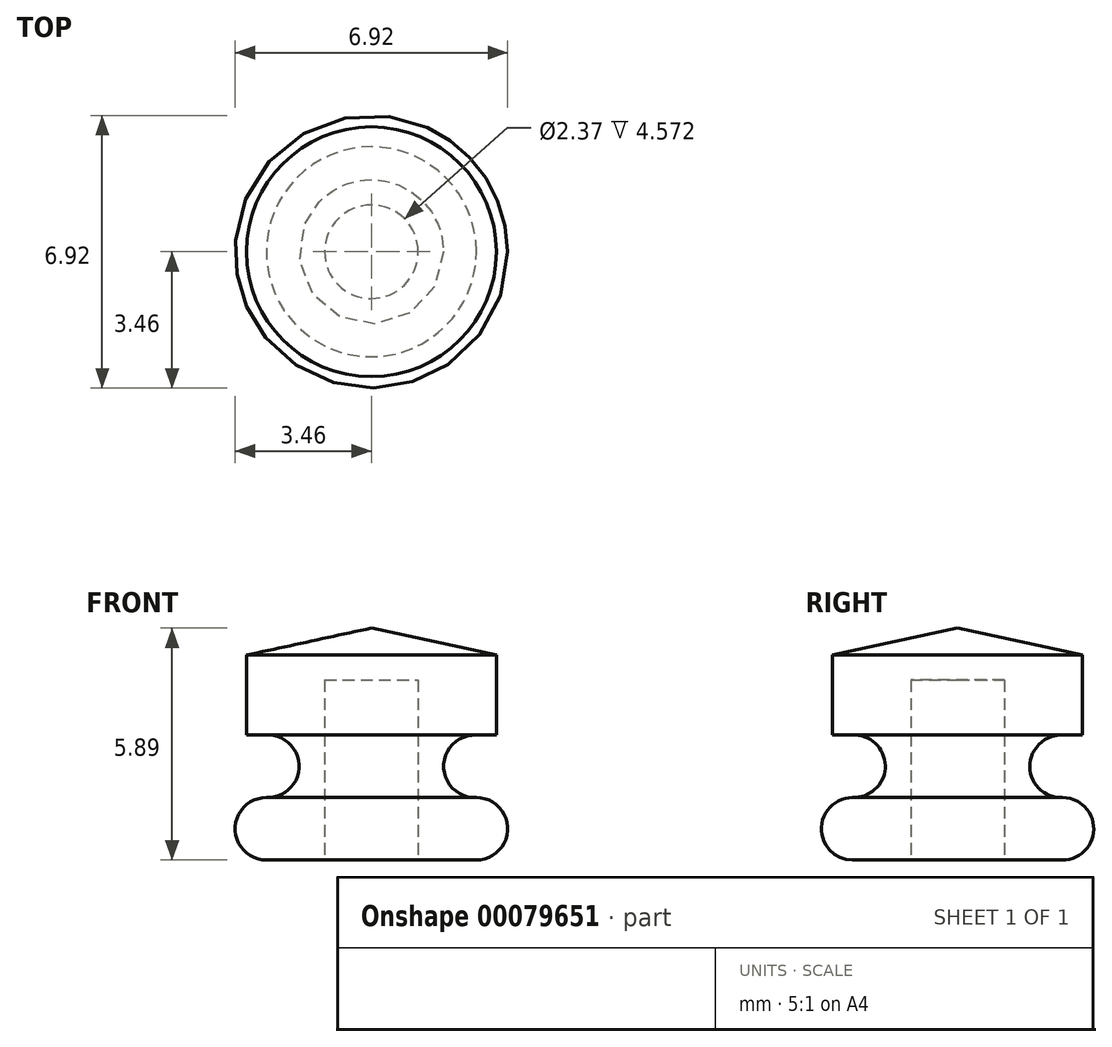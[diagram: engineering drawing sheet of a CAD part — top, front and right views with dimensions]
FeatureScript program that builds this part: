
annotation { "Feature Type Name" : "Feature", "Feature Type Description" : "" }
export const myFeature = defineFeature(function(context is Context, id is Id, definition is map)
    precondition{}
    {
        {
            var Q0;
            Q0=qCreatedBy(makeId("Front.planeOp"),FACE);
            var sketch = newSketch(context, id + "F0", { "sketchPlane" : qUnion([Q0])});
            skLineSegment(sketch, "E0", {"start": v(0, 13.12) * mm, "end": v(0, -12.35) * mm, "construction": true});
            skLineSegment(sketch, "E1", {"start": v(0, 1.69) * mm, "end": v(0, -4.2) * mm});
            skLineSegment(sketch, "E2", {"start": v(0, -4.2) * mm, "end": v(-2.67, -4.2) * mm});
            skArc(sketch, "E3", {"start": v(-2.67, -2.62) * mm, "mid": v(-3.46, -3.4) * mm, "end": v(-2.67, -4.2) * mm});
            skArc(sketch, "E4", {"start": v(-2.67, -2.62) * mm, "mid": v(-1.83, -1.82) * mm, "end": v(-2.67, -1.03) * mm});
            skLineSegment(sketch, "E5", {"start": v(-2.67, -1.03) * mm, "end": v(0, -1.03) * mm, "construction": true});
            skLineSegment(sketch, "E6", {"start": v(-2.67, -1.03) * mm, "end": v(-3.17, -1.03) * mm});
            skLineSegment(sketch, "E7", {"start": v(-3.17, -1.03) * mm, "end": v(-3.17, 1) * mm});
            skLineSegment(sketch, "E8", {"start": v(-3.17, 1) * mm, "end": v(0, 1.69) * mm});
            skSolve(sketch);
        }
        {
            var Q0;
            Q0=makeQuery(id+"F0.imprint","IMPRINT",FACE,{"disambiguationData":[TD([[makeQuery(id+"F0.imprint","IMPRINT",EDGE,{"derivedFrom":sQuery(id+"F0.wireOp",EDGE,"E2")}),-1.0]])]});
            var Q1;
            Q1=sQuery(id+"F0.wireOp",EDGE,"E0");
            revolve(context, id + "F1", {"entities" : qUnion([Q0]), "axis" : qUnion([Q1]), "revolveType" : RevolveType.FULL});
        }
        {
            var Q0;
            Q0=makeQuery(id+"F1.opRevolve","SWEPT_FACE",FACE,{"disambiguationData":[OSD([sQuery(id+"F0.wireOp",EDGE,"E2")])]});
            var sketch = newSketch(context, id + "F2", { "sketchPlane" : qUnion([Q0])});
            skCircle(sketch, "E9", {"center": v(0, 0) * mm, "radius": 1.19 * mm});
            skSolve(sketch);
        }
        {
            var Q0;
            Q0 = qSketchRegion(id + "F2", true);
            extrude(context, id + "F3", {"entities" : qUnion([Q0]), "operationType" : NewBodyOperationType.REMOVE, "oppositeDirection" : true, "depth" : 4.57 * mm});
        }
    });
